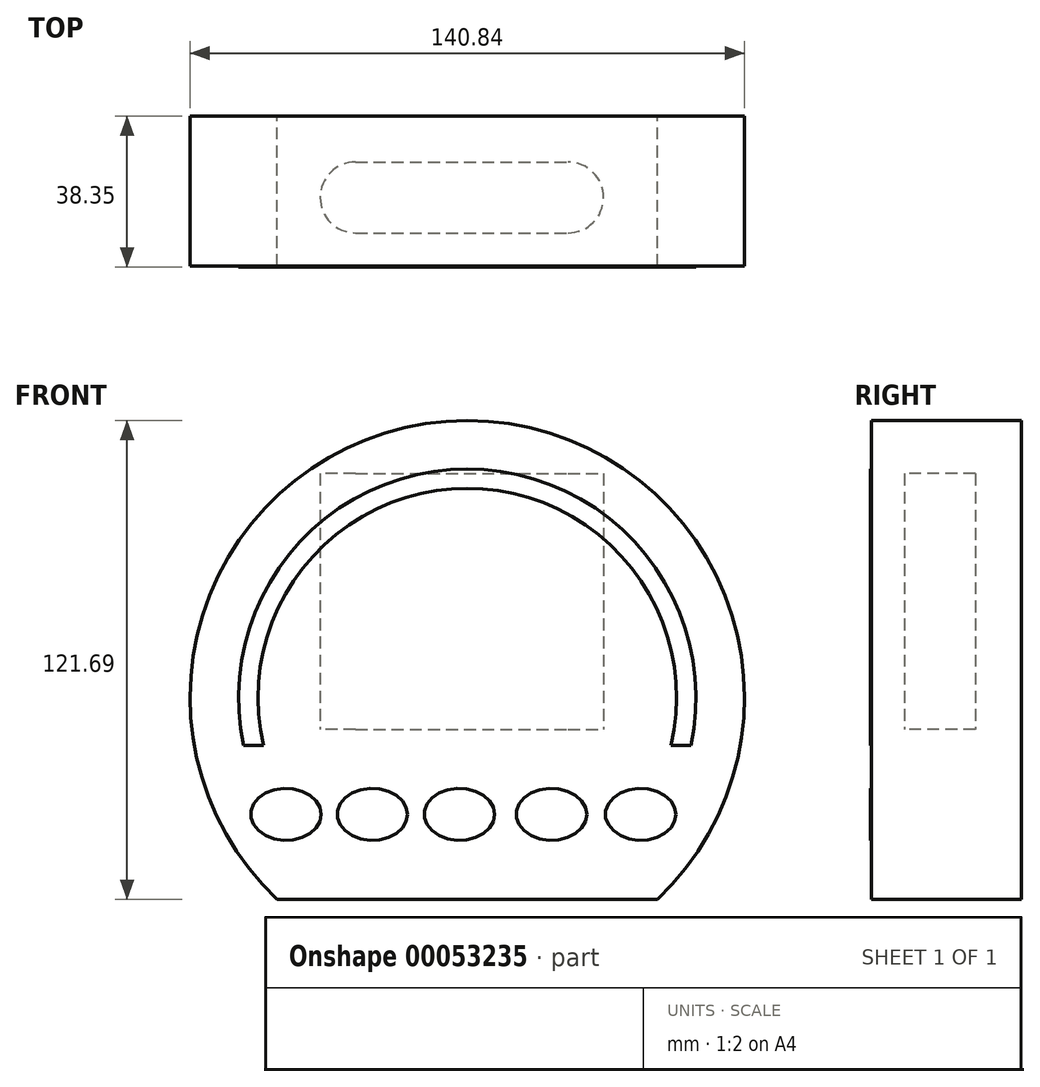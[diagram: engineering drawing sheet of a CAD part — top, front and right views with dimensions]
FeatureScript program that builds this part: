
annotation { "Feature Type Name" : "Feature", "Feature Type Description" : "" }
export const myFeature = defineFeature(function(context is Context, id is Id, definition is map)
    precondition{}
    {
        {
            var Q0;
            Q0=qCreatedBy(makeId("Front.planeOp"),FACE);
            var sketch = newSketch(context, id + "F0", { "sketchPlane" : qUnion([Q0])});
            skArc(sketch, "E0", {"start": v(-48.28, -43.18) * mm, "mid": v(0, 78.5) * mm, "end": v(48.28, -43.18) * mm});
            skLineSegment(sketch, "E1", {"start": v(-48.28, -43.18) * mm, "end": v(48.28, -43.18) * mm});
            skSolve(sketch);
        }
        {
            var Q0;
            Q0 = qSketchRegion(id + "F0", true);
            extrude(context, id + "F1", {"entities" : qUnion([Q0]), "depth" : 38.1 * mm});
        }
        {
            var Q0;
            Q0=makeQuery(id+"F1.opExtrude","CAP_FACE",FACE,{"disambiguationData":[OSD([sQuery(id+"F0.wireOp",EDGE,"E0"),sQuery(id+"F0.wireOp",EDGE,"E1")])],"isStart":false});
            var sketch = newSketch(context, id + "F2", { "sketchPlane" : qUnion([Q0])});
            skEllipse(sketch, "E2", {"center": v(-46.05, -21.53) * mm, "majorRadius": 8.96 * mm, "minorRadius": 6.6 * mm, "majorAxis": v(1, 0)});
            skEllipse(sketch, "E3", {"center": v(-24.14, -21.53) * mm, "majorRadius": 8.96 * mm, "minorRadius": 6.6 * mm, "majorAxis": v(1, 0)});
            skEllipse(sketch, "E4", {"center": v(-2, -21.53) * mm, "majorRadius": 8.96 * mm, "minorRadius": 6.6 * mm, "majorAxis": v(1, 0)});
            skEllipse(sketch, "E5", {"center": v(21.4, -21.53) * mm, "majorRadius": 8.96 * mm, "minorRadius": 6.6 * mm, "majorAxis": v(1, 0)});
            skEllipse(sketch, "E6", {"center": v(44.05, -21.53) * mm, "majorRadius": 8.96 * mm, "minorRadius": 6.6 * mm, "majorAxis": v(1, 0)});
            skArc(sketch, "E7", {"start": v(-56.8, -4.1) * mm, "mid": v(0, 66.18) * mm, "end": v(56.8, -4.1) * mm});
            skArc(sketch, "E8", {"start": v(-51.76, -4.1) * mm, "mid": v(0, 61.27) * mm, "end": v(51.76, -4.1) * mm});
            skLineSegment(sketch, "E9", {"start": v(-56.8, -4.1) * mm, "end": v(-51.76, -4.1) * mm});
            skLineSegment(sketch, "E10", {"start": v(51.76, -4.1) * mm, "end": v(56.8, -4.1) * mm});
            skSolve(sketch);
        }
        {
            var Q0;
            Q0 = qSketchRegion(id + "F2", true);
            extrude(context, id + "F3", {"entities" : qUnion([Q0]), "operationType" : NewBodyOperationType.ADD, "depth" : 0.25 * mm});
        }
        {
            var Q0;
            Q0=qCreatedBy(makeId("Top.planeOp"),FACE);
            var sketch = newSketch(context, id + "F4", { "sketchPlane" : qUnion([Q0])});
            skCircle(sketch, "E11", {"center": v(-28.38, -20.7) * mm, "radius": 9 * mm});
            skCircle(sketch, "E12", {"center": v(-10.38, -20.7) * mm, "radius": 9 * mm});
            skCircle(sketch, "E13", {"center": v(7.62, -20.7) * mm, "radius": 9 * mm});
            skCircle(sketch, "E14", {"center": v(25.62, -20.7) * mm, "radius": 9 * mm});
            skLineSegment(sketch, "E15", {"start": v(-28.38, -11.7) * mm, "end": v(25.62, -11.7) * mm});
            skLineSegment(sketch, "E16", {"start": v(-28.38, -29.7) * mm, "end": v(25.62, -29.7) * mm});
            skSolve(sketch);
        }
        {
            var Q0;
            Q0 = qSketchRegion(id + "F4", true);
            extrude(context, id + "F5", {"entities" : qUnion([Q0]), "depth" : 65 * mm});
        }
    });
